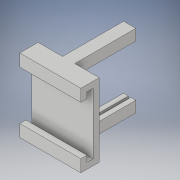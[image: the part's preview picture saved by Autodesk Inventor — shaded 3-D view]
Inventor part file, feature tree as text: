
AUTODESK INVENTOR PART (.ipt)
format: ipt  version: 2019 (Build 230136000, 136)  size: 167,424 bytes
history: native  units: mm
features: extrude x6, sketch x6, mirror x1
ambient origin geometry x8: Origin, YZ Plane, XZ Plane, XY Plane, X Axis, Y Axis, Z Axis, Center Point
bodies: Solid1 (feature_tree)
feature tree (13):
  extrude  "Extrusion1"  Depth=60.0mm
  extrude  "Extrusion2"  Depth=30.0mm
  extrude  "Extrusion3"  Depth=5.0mm
  extrude  "Extrusion4"  Depth=5.0mm
  extrude  "Extrusion5"  Depth=5.0mm
  extrude  "Extrusion12"  Depth=5.0mm
  mirror  "Mirror1"
  sketch  "Sketch1"  dims[d0=50.0mm d1=60.0mm]
  sketch  "Sketch2"  dims[d2=30.0mm d3=25.0mm]
  sketch  "Sketch3"  dims[d4=5.0mm d5=0.0mm d6=5.0mm]
  sketch  "Sketch4"  dims[d7=10.0mm d8=0.0mm d9=5.0mm]
  sketch  "Sketch5"  dims[d10=10.0mm d11=0.0mm d12=5.0mm]
  sketch  "Sketch12"  dims[d13=5.0mm d14=0.0mm d15=5.0mm d16=5.0mm d17=0.0mm d42=10.0mm d43=5.0mm d44=20.0mm d45=4.0mm d46=4.0mm d47=4.0mm d48=50.0mm d49=0.0mm d50=4.0mm]
